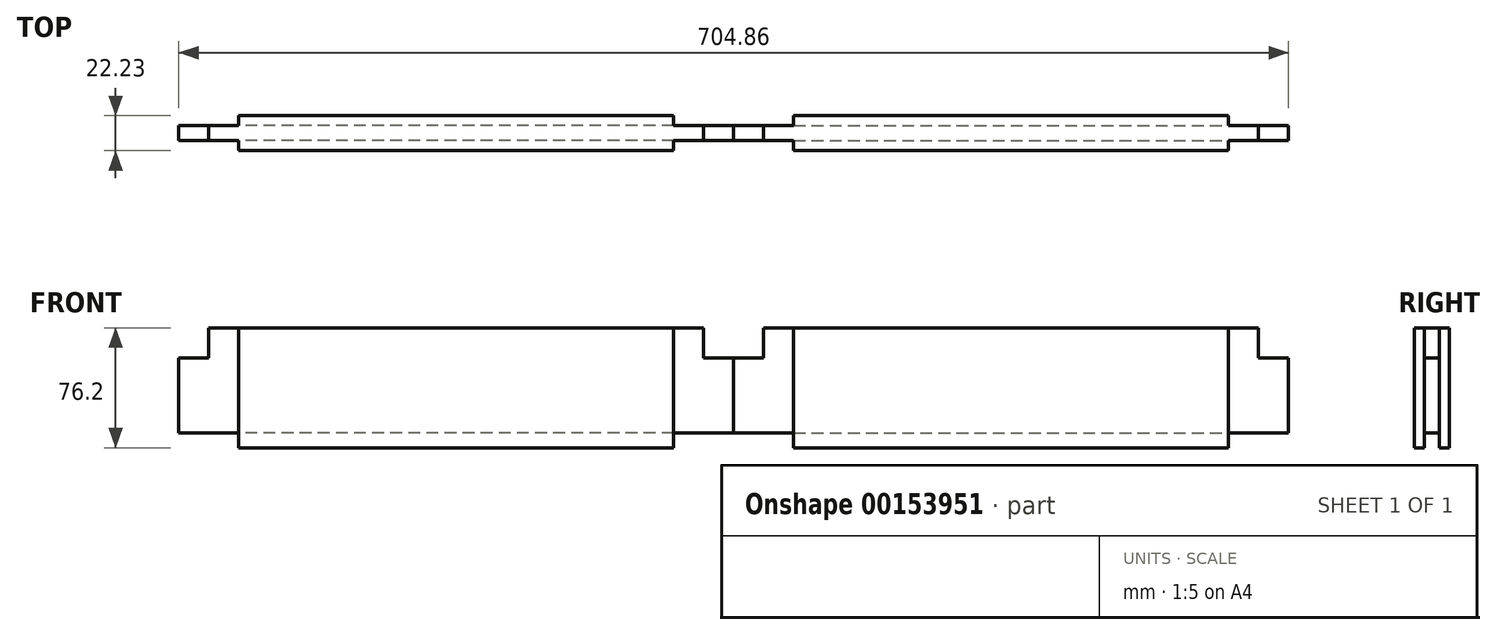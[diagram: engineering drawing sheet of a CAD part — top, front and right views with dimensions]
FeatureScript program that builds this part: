
annotation { "Feature Type Name" : "Feature", "Feature Type Description" : "" }
export const myFeature = defineFeature(function(context is Context, id is Id, definition is map)
    precondition{}
    {
        {
            var Q0;
            Q0=qCreatedBy(makeId("Front.planeOp"),FACE);
            var sketch = newSketch(context, id + "F0", { "sketchPlane" : qUnion([Q0])});
            skLineSegment(sketch, "E0.bottom", {"start": v(0, 0) * mm, "end": v(352.43, 0) * mm});
            skLineSegment(sketch, "E0.top", {"start": v(0, 76.2) * mm, "end": v(352.43, 76.2) * mm});
            skLineSegment(sketch, "E0.left", {"start": v(0, 0) * mm, "end": v(0, 76.2) * mm});
            skLineSegment(sketch, "E0.right", {"start": v(352.43, 0) * mm, "end": v(352.43, 76.2) * mm});
            skSolve(sketch);
        }
        {
            var Q0;
            Q0=makeQuery(id+"F0.imprint","IMPRINT",FACE,{"disambiguationData":[TD([[makeQuery(id+"F0.imprint","IMPRINT",EDGE,{"derivedFrom":sQuery(id+"F0.wireOp",EDGE,"E0.bottom")}),1.0]])]});
            extrude(context, id + "F1", {"entities" : qUnion([Q0]), "depth" : 22.22 * mm});
        }
        {
            var Q0;
            Q0=makeQuery(id+"F1.opExtrude","SWEPT_FACE",FACE,{"disambiguationData":[OSD([sQuery(id+"F0.wireOp",EDGE,"E0.bottom")])]});
            var sketch = newSketch(context, id + "F2", { "sketchPlane" : qUnion([Q0])});
            skLineSegment(sketch, "E1.bottom", {"start": v(0, 15.88) * mm, "end": v(352.43, 15.88) * mm});
            skLineSegment(sketch, "E1.top", {"start": v(0, 6.35) * mm, "end": v(352.43, 6.35) * mm});
            skLineSegment(sketch, "E1.left", {"start": v(0, 15.88) * mm, "end": v(0, 6.35) * mm});
            skLineSegment(sketch, "E1.right", {"start": v(352.43, 15.88) * mm, "end": v(352.43, 6.35) * mm});
            skLineSegment(sketch, "E2", {"start": v(38.1, 0) * mm, "end": v(38.1, 22.23) * mm});
            skLineSegment(sketch, "E3", {"start": v(314.32, 22.23) * mm, "end": v(314.32, 0) * mm});
            skSolve(sketch);
        }
        {
            var Q0;
            {var subQ0=sQuery(id+"F2.wireOp",EDGE,"E1.right");Q0=makeQuery(id+"F2.imprint","IMPRINT",FACE,{"disambiguationData":[TD([[makeQuery(id+"F2.imprint","IMPRINT",EDGE,{"derivedFrom":subQ0}),-1.0]])]});}
            var Q1;
            {var subQ0=sQuery(id+"F2.wireOp",EDGE,"E2");var subQ1=sQuery(id+"F2.wireOp",EDGE,"E1.bottom");var subQ2=makeQuery(id+"F2.imprint","INTERSECT",VERTEX,{"derivedFrom":[subQ1,subQ0]});Q1=makeQuery(id+"F2.imprint","IMPRINT",FACE,{"disambiguationData":[TD([[makeQuery(id+"F2.imprint","IMPRINT",EDGE,{"disambiguationData":[TD([[subQ2,-1.0]])],"derivedFrom":subQ1}),-1.0]])]});}
            var Q2;
            {var subQ0=sQuery(id+"F2.wireOp",EDGE,"E1.left");Q2=makeQuery(id+"F2.imprint","IMPRINT",FACE,{"disambiguationData":[TD([[makeQuery(id+"F2.imprint","IMPRINT",EDGE,{"derivedFrom":subQ0}),1.0]])]});}
            extrude(context, id + "F3", {"entities" : qUnion([Q0, Q1, Q2]), "operationType" : NewBodyOperationType.REMOVE, "oppositeDirection" : true, "depth" : 9.52 * mm});
        }
        {
            var Q0;
            {var subQ1=sQuery(id+"F0.wireOp",EDGE,"E0.bottom");var subQ4=sQuery(id+"F2.wireOp",EDGE,"E2");var subQ6=makeQuery(id+"F1.opExtrude","CAP_EDGE",EDGE,{"disambiguationData":[OSD([subQ1])],"isStart":false});var subQ7=makeQuery(id+"F2.imprint","INTERSECT",VERTEX,{"derivedFrom":[subQ6,subQ4]});Q0=makeQuery(id+"F2.imprint","IMPRINT",FACE,{"disambiguationData":[TD([[makeQuery(id+"F2.imprint","IMPRINT",EDGE,{"disambiguationData":[TD([[subQ7,1.0]])],"derivedFrom":subQ4}),1.0]])]});}
            var Q1;
            {var subQ1=sQuery(id+"F0.wireOp",EDGE,"E0.bottom");var subQ4=sQuery(id+"F2.wireOp",EDGE,"E3");var subQ6=makeQuery(id+"F1.opExtrude","CAP_EDGE",EDGE,{"disambiguationData":[OSD([subQ1])],"isStart":false});var subQ7=makeQuery(id+"F2.imprint","INTERSECT",VERTEX,{"derivedFrom":[subQ6,subQ4]});Q1=makeQuery(id+"F2.imprint","IMPRINT",FACE,{"disambiguationData":[TD([[makeQuery(id+"F2.imprint","IMPRINT",EDGE,{"disambiguationData":[TD([[subQ7,-1.0]])],"derivedFrom":subQ4}),1.0]])]});}
            var Q2;
            {var subQ1=sQuery(id+"F0.wireOp",EDGE,"E0.bottom");var subQ4=sQuery(id+"F2.wireOp",EDGE,"E3");var subQ6=makeQuery(id+"F1.opExtrude","CAP_EDGE",EDGE,{"disambiguationData":[OSD([subQ1])],"isStart":true});var subQ7=makeQuery(id+"F2.imprint","INTERSECT",VERTEX,{"derivedFrom":[subQ6,subQ4]});Q2=makeQuery(id+"F2.imprint","IMPRINT",FACE,{"disambiguationData":[TD([[makeQuery(id+"F2.imprint","IMPRINT",EDGE,{"disambiguationData":[TD([[subQ7,1.0]])],"derivedFrom":subQ4}),1.0]])]});}
            var Q3;
            {var subQ1=sQuery(id+"F0.wireOp",EDGE,"E0.bottom");var subQ4=sQuery(id+"F2.wireOp",EDGE,"E2");var subQ6=makeQuery(id+"F1.opExtrude","CAP_EDGE",EDGE,{"disambiguationData":[OSD([subQ1])],"isStart":true});var subQ7=makeQuery(id+"F2.imprint","INTERSECT",VERTEX,{"derivedFrom":[subQ6,subQ4]});Q3=makeQuery(id+"F2.imprint","IMPRINT",FACE,{"disambiguationData":[TD([[makeQuery(id+"F2.imprint","IMPRINT",EDGE,{"disambiguationData":[TD([[subQ7,-1.0]])],"derivedFrom":subQ4}),1.0]])]});}
            extrude(context, id + "F4", {"entities" : qUnion([Q0, Q1, Q2, Q3]), "operationType" : NewBodyOperationType.REMOVE, "endBound" : BoundingType.UP_TO_NEXT, "oppositeDirection" : true, "depth" : 9.52 * mm});
        }
        {
            var Q0;
            {var subQ0=sQuery(id+"F2.wireOp",EDGE,"E1.top");Q0=makeQuery(id+"F4.boolean.opBoolean","COPY",FACE,{"derivedFrom":makeQuery(id+"F4.opExtrude","SWEPT_FACE",FACE,{"disambiguationData":[OSD([subQ0]),TDD([makeQuery(id+"F2.imprint","IMPRINT",EDGE,{"disambiguationData":[TD([[makeQuery(id+"F2.imprint","INTERSECT",VERTEX,{"derivedFrom":[subQ0,sQuery(id+"F2.wireOp",EDGE,"E2")]}),1.0]])],"derivedFrom":subQ0})])]})});}
            var sketch = newSketch(context, id + "F5", { "sketchPlane" : qUnion([Q0])});
            skLineSegment(sketch, "E4.bottom", {"start": v(0, 76.2) * mm, "end": v(-19.05, 76.2) * mm});
            skLineSegment(sketch, "E4.top", {"start": v(0, 57.15) * mm, "end": v(-19.05, 57.15) * mm});
            skLineSegment(sketch, "E4.left", {"start": v(0, 76.2) * mm, "end": v(0, 57.15) * mm});
            skLineSegment(sketch, "E4.right", {"start": v(-19.05, 76.2) * mm, "end": v(-19.05, 57.15) * mm});
            skLineSegment(sketch, "E5.bottom", {"start": v(-333.38, 76.2) * mm, "end": v(-352.43, 76.2) * mm});
            skLineSegment(sketch, "E5.top", {"start": v(-333.38, 57.15) * mm, "end": v(-352.43, 57.15) * mm});
            skLineSegment(sketch, "E5.left", {"start": v(-333.38, 76.2) * mm, "end": v(-333.38, 57.15) * mm});
            skLineSegment(sketch, "E5.right", {"start": v(-352.43, 76.2) * mm, "end": v(-352.43, 57.15) * mm});
            skSolve(sketch);
        }
        {
            var Q0;
            Q0=makeQuery(id+"F5.imprint","IMPRINT",FACE,{"disambiguationData":[TD([[makeQuery(id+"F5.imprint","IMPRINT",EDGE,{"derivedFrom":sQuery(id+"F5.wireOp",EDGE,"E5.bottom")}),1.0]])]});
            var Q1;
            Q1=makeQuery(id+"F5.imprint","IMPRINT",FACE,{"disambiguationData":[TD([[makeQuery(id+"F5.imprint","IMPRINT",EDGE,{"derivedFrom":sQuery(id+"F5.wireOp",EDGE,"E4.bottom")}),1.0]])]});
            extrude(context, id + "F6", {"entities" : qUnion([Q0, Q1]), "operationType" : NewBodyOperationType.REMOVE, "endBound" : BoundingType.UP_TO_NEXT, "oppositeDirection" : true, "depth" : 9.52 * mm});
        }
        {
            var Q0;
            Q0=makeQuery(id+"F1.opExtrude","SWEPT_BODY",BODY,{"disambiguationData":[OSD([sQuery(id+"F0.wireOp",EDGE,"E0.bottom"),sQuery(id+"F0.wireOp",EDGE,"E0.top"),sQuery(id+"F0.wireOp",EDGE,"E0.left"),sQuery(id+"F0.wireOp",EDGE,"E0.right")])]});
            var Q1;
            Q1=qCreatedBy(makeId("Right.planeOp"),FACE);
            mirror(context, id + "F7", {"entities" : qUnion([Q0]), "mirrorPlane" : qUnion([Q1])});
        }
    });
